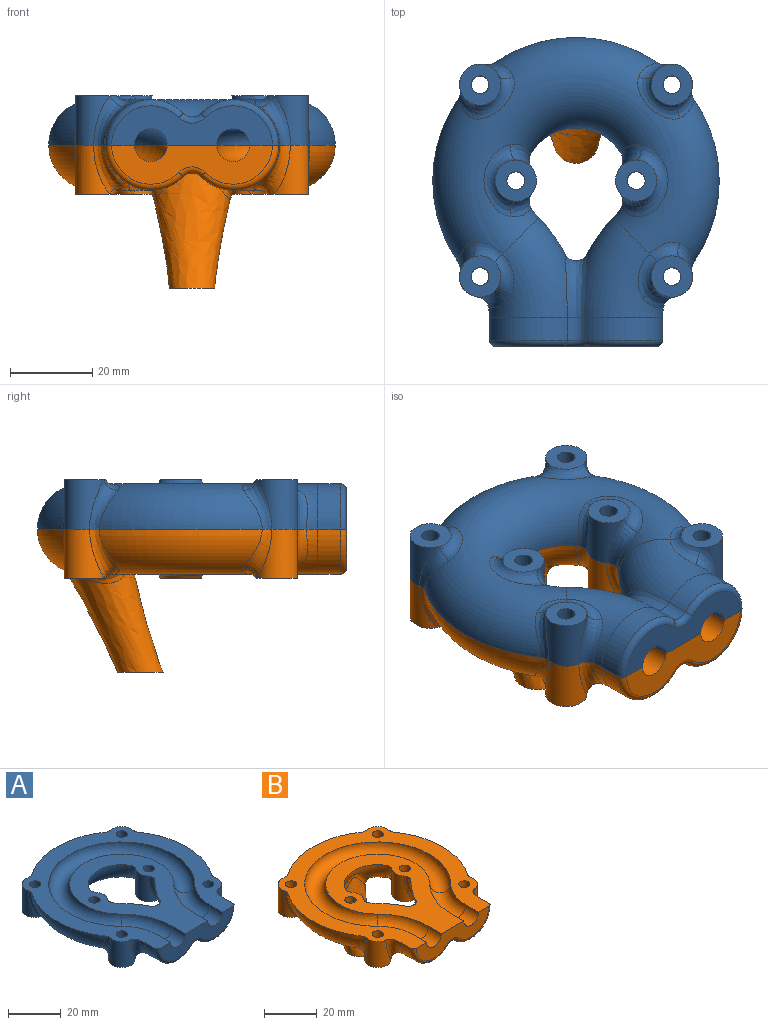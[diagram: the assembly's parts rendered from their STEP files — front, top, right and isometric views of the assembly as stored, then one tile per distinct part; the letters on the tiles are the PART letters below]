
ASSEMBLY  parts=2 mates=1
PART A: 56 faces, bbox 75.6x78.3x20.8 mm
  f0: plane 60.28x39.81mm, normal (0,0,1), area 970.4mm2, adj f2,f3,f4,f6,f7,f8,f9,f10
  f1: plane 75.05x69.58mm, normal (0,0,1), area 1332.3mm2, adj f2,f3,f4,f5,f6,f7,f8,f9
  f2: torus R=23.77mm, axis (0,0,-1), area 2757.4mm2, adj f0,f1,f3,f7,f33,f34,f37,f38
  f3: torus R=23.23mm, axis (0,0,1), area 401.1mm2, adj f0,f1,f2,f11,f35,f36,f40
  f4: plane 39x9.5mm, normal (0,-1,0), area 245.2mm2, adj f0,f1,f6,f12,f53,f54,f55
  f5: cylinder r=11mm len=18.86mm, axis (0,1,0), area 143.2mm2, adj f1,f7,f39,f53
  f6: cylinder r=4mm len=8mm, axis (0,1,0), area 88mm2, adj f0,f1,f4,f8
  f7: torus R=23.23mm, axis (0,0,1), area 401.1mm2, adj f0,f1,f2,f5,f31,f32,f40
  f8: torus R=23.23mm, axis (0,0,1), area 229.3mm2, adj f0,f1,f6,f9
  f9: torus R=23.77mm, axis (0,0,-1), area 1407.4mm2, adj f0,f1,f8,f10
  f10: torus R=23.23mm, axis (0,0,1), area 229.3mm2, adj f0,f1,f9,f12
  f11: cylinder r=11mm len=18.86mm, axis (0,-1,0), area 143.2mm2, adj f1,f3,f39,f55
  f12: cylinder r=4mm len=8mm, axis (0,-1,0), area 88mm2, adj f0,f1,f4,f10
  f13: cylinder r=5mm len=12mm, axis (0,0,1), area 156.2mm2, adj f1,f14,f50,f52
  f14: plane 10.36x10.36mm, normal (0,0,-1), area 64mm2, adj f13,f30,f51
  f15: cylinder r=5mm len=12mm, axis (0,0,1), area 133.3mm2, adj f1,f16,f35,f38
  f16: plane 10.38x10.38mm, normal (0,0,-1), area 64mm2, adj f15,f29,f36,f37
  f17: cylinder r=5mm len=12mm, axis (0,0,1), area 156.2mm2, adj f1,f18,f47,f49
  f18: plane 10.36x10.36mm, normal (0,0,-1), area 64mm2, adj f17,f28,f48
  f19: cylinder r=5mm len=12mm, axis (0,0,1), area 133.3mm2, adj f1,f20,f31,f34
  f20: plane 10.38x10.38mm, normal (0,0,-1), area 64mm2, adj f19,f27,f32,f33
  f21: cylinder r=5mm len=12mm, axis (0,0,1), area 111.7mm2, adj f0,f22,f44,f46
  f22: plane 10.39x10.39mm, normal (0,0,-1), area 64mm2, adj f21,f26,f45
  f23: cylinder r=5mm len=12mm, axis (0,0,1), area 111.7mm2, adj f0,f24,f41,f43
  f24: plane 10.39x10.39mm, normal (0,0,-1), area 64mm2, adj f23,f25,f42
  f25: cylinder r=2.15mm len=12mm, axis (0,0,1), area 162.1mm2, adj f0,f24
  f26: cylinder r=2.15mm len=12mm, axis (0,0,1), area 162.1mm2, adj f0,f22
  f27: cylinder r=2.15mm len=12mm, axis (0,0,1), area 162.1mm2, adj f1,f20
  f28: cylinder r=2.15mm len=12mm, axis (0,0,1), area 162.1mm2, adj f1,f18
  f29: cylinder r=2.15mm len=12mm, axis (0,0,1), area 162.1mm2, adj f1,f16
  f30: cylinder r=2.15mm len=12mm, axis (0,0,1), area 162.1mm2, adj f1,f14
  f31: bspline ~14.01x8.25mm, area 52.2mm2, adj f1,f7,f19,f32
  f32: bspline ~10.86x4.77mm, area 35.4mm2, adj f7,f20,f31,f33
  f33: bspline ~8.15x5.06mm, area 24.6mm2, adj f2,f20,f32,f34
  f34: bspline ~14.58x7.27mm, area 41.1mm2, adj f1,f2,f19,f33
  f35: bspline ~14.01x8.25mm, area 52.2mm2, adj f1,f3,f15,f36
  f36: bspline ~10.86x4.77mm, area 35.4mm2, adj f3,f16,f35,f37
  f37: bspline ~8.15x5.06mm, area 24.6mm2, adj f2,f16,f36,f38
  f38: bspline ~13.38x7.26mm, area 41.1mm2, adj f1,f2,f15,f37
  f39: cylinder r=3mm len=5.5mm, axis (0,1,0), area 26.3mm2, adj f5,f11,f40,f54
  f40: bspline ~17.07x8mm, area 95.7mm2, adj f0,f3,f7,f39
  f41: bspline ~13.11x6.17mm, area 51.8mm2, adj f0,f2,f23,f42
  f42: bspline ~17.49x7.8mm, area 70.2mm2, adj f2,f24,f41,f43
  f43: bspline ~13.83x6.12mm, area 51.8mm2, adj f0,f2,f23,f42
  f44: bspline ~12.91x5.98mm, area 51.8mm2, adj f0,f2,f21,f45
  f45: bspline ~17.49x7.8mm, area 70.2mm2, adj f2,f22,f44,f46
  f46: bspline ~14.07x6.28mm, area 51.8mm2, adj f0,f2,f21,f45
  f47: bspline ~13.12x7.1mm, area 41.1mm2, adj f1,f2,f17,f48
  f48: bspline ~10.75x10.58mm, area 49.3mm2, adj f2,f18,f47,f49
  f49: bspline ~13.53x7.19mm, area 41.1mm2, adj f1,f2,f17,f48
  f50: bspline ~13.12x7.1mm, area 41.1mm2, adj f1,f2,f13,f51
  f51: bspline ~10.75x10.58mm, area 49.3mm2, adj f2,f14,f50,f52
  f52: bspline ~13.53x7.2mm, area 41.1mm2, adj f1,f2,f13,f51
  f53: torus R=9.5mm, axis (0,1,0), area 58.3mm2, adj f1,f4,f5,f54
  f54: torus R=4.5mm, axis (0,1,0), area 13.3mm2, adj f4,f39,f53,f55
  f55: torus R=9.5mm, axis (0,1,0), area 58.3mm2, adj f1,f4,f11,f54
PART B: 59 faces, bbox 75.6x78.3x43 mm
  f0: plane 60.28x39.81mm, normal (0,0,1), area 970.4mm2, adj f2,f3,f4,f6,f7,f8,f9,f10
  f1: plane 75.05x69.58mm, normal (0,0,1), area 1332.3mm2, adj f2,f3,f4,f5,f6,f7,f8,f9
  f2: torus R=23.77mm, axis (0,0,-1), area 2365.6mm2, adj f0,f1,f3,f7,f33,f34,f37,f38
  f3: torus R=23.23mm, axis (0,0,1), area 410.3mm2, adj f0,f1,f2,f11,f35,f36,f40
  f4: plane 39x9.5mm, normal (0,-1,0), area 245.2mm2, adj f0,f1,f6,f12,f56,f57,f58
  f5: cylinder r=11mm len=18.86mm, axis (0,1,0), area 143.2mm2, adj f1,f7,f39,f56
  f6: cylinder r=4mm len=8mm, axis (0,1,0), area 88mm2, adj f0,f1,f4,f8
  f7: torus R=23.23mm, axis (0,0,1), area 410.3mm2, adj f0,f1,f2,f5,f31,f32,f40
  f8: torus R=23.23mm, axis (0,0,1), area 229.3mm2, adj f0,f1,f6,f9
  f9: torus R=23.77mm, axis (0,0,-1), area 1407.4mm2, adj f0,f1,f8,f10
  f10: torus R=23.23mm, axis (0,0,1), area 229.3mm2, adj f0,f1,f9,f12
  f11: cylinder r=11mm len=18.86mm, axis (0,-1,0), area 143.2mm2, adj f1,f3,f39,f58
  f12: cylinder r=4mm len=8mm, axis (0,-1,0), area 88mm2, adj f0,f1,f4,f10
  f13: cylinder r=5mm len=12mm, axis (0,0,1), area 156.2mm2, adj f1,f14,f50,f52
  f14: plane 10.36x10.36mm, normal (0,0,-1), area 64mm2, adj f13,f30,f51
  f15: cylinder r=5mm len=12mm, axis (0,0,1), area 133.3mm2, adj f1,f16,f35,f38
  f16: plane 10.38x10.38mm, normal (0,0,-1), area 64mm2, adj f15,f29,f36,f37
  f17: cylinder r=5mm len=12mm, axis (0,0,1), area 156.2mm2, adj f1,f18,f47,f49
  f18: plane 10.36x10.36mm, normal (0,0,-1), area 64mm2, adj f17,f28,f48
  f19: cylinder r=5mm len=12mm, axis (0,0,1), area 133.3mm2, adj f1,f20,f31,f34
  f20: plane 10.38x10.38mm, normal (0,0,-1), area 64mm2, adj f19,f27,f32,f33
  f21: cylinder r=5mm len=12mm, axis (0,0,1), area 111.7mm2, adj f0,f22,f44,f46
  f22: plane 10.39x10.39mm, normal (0,0,-1), area 64mm2, adj f21,f26,f45
  f23: cylinder r=5mm len=12mm, axis (0,0,1), area 111.7mm2, adj f0,f24,f41,f43
  f24: plane 10.39x10.39mm, normal (0,0,-1), area 64mm2, adj f23,f25,f42
  f25: cylinder r=2.15mm len=12mm, axis (0,0,1), area 162.1mm2, adj f0,f24
  f26: cylinder r=2.15mm len=12mm, axis (0,0,1), area 162.1mm2, adj f0,f22
  f27: cylinder r=2.15mm len=12mm, axis (0,0,1), area 162.1mm2, adj f1,f20
  f28: cylinder r=2.15mm len=12mm, axis (0,0,1), area 162.1mm2, adj f1,f18
  f29: cylinder r=2.15mm len=12mm, axis (0,0,1), area 162.1mm2, adj f1,f16
  f30: cylinder r=2.15mm len=12mm, axis (0,0,1), area 162.1mm2, adj f1,f14
  f31: bspline ~14.01x8.25mm, area 52.2mm2, adj f1,f7,f19,f32
  f32: bspline ~10.86x4.77mm, area 35.4mm2, adj f7,f20,f31,f33
  f33: bspline ~8.15x5.06mm, area 24.6mm2, adj f2,f20,f32,f34
  f34: bspline ~14.58x7.27mm, area 41.1mm2, adj f1,f2,f19,f33
  f35: bspline ~14.01x8.25mm, area 52.2mm2, adj f1,f3,f15,f36
  f36: bspline ~10.86x4.77mm, area 35.4mm2, adj f3,f16,f35,f37
  f37: bspline ~8.15x5.06mm, area 24.6mm2, adj f2,f16,f36,f38
  f38: bspline ~13.38x7.26mm, area 41.1mm2, adj f1,f2,f15,f37
  f39: cylinder r=3mm len=5.5mm, axis (0,1,0), area 26.3mm2, adj f5,f11,f40,f57
  f40: bspline ~17.07x8mm, area 95.7mm2, adj f0,f3,f7,f39
  f41: bspline ~13.11x6.17mm, area 51.8mm2, adj f0,f2,f23,f42
  f42: bspline ~17.49x7.8mm, area 70.2mm2, adj f2,f24,f41,f43
  f43: bspline ~13.83x6.12mm, area 51.8mm2, adj f0,f2,f23,f42
  f44: bspline ~12.91x5.98mm, area 51.8mm2, adj f0,f2,f21,f45
  f45: bspline ~17.49x7.8mm, area 70.2mm2, adj f2,f22,f44,f46
  f46: bspline ~14.07x6.28mm, area 51.8mm2, adj f0,f2,f21,f45
  f47: bspline ~13.12x7.1mm, area 41.1mm2, adj f1,f2,f17,f48
  f48: bspline ~10.75x10.58mm, area 49.3mm2, adj f2,f18,f47,f49
  f49: bspline ~13.53x7.19mm, area 41.1mm2, adj f1,f2,f17,f48
  f50: bspline ~13.12x7.1mm, area 41.1mm2, adj f1,f2,f13,f51
  f51: bspline ~10.75x10.58mm, area 49.3mm2, adj f2,f14,f50,f52
  f52: bspline ~13.53x7.2mm, area 41.1mm2, adj f1,f2,f13,f51
  f53: bspline ~31.3x27.46mm, area 1113.2mm2, adj f54,f55
  f54: plane 11.02x11.02mm, normal (0,0,-1), area 95mm2, adj f53
  f55: bspline ~24.99x16.32mm, area 200.8mm2, adj f2,f53
  f56: torus R=9.5mm, axis (0,1,0), area 58.3mm2, adj f1,f4,f5,f57
  f57: torus R=4.5mm, axis (0,1,0), area 13.3mm2, adj f4,f39,f56,f58
  f58: torus R=9.5mm, axis (0,1,0), area 58.3mm2, adj f1,f4,f11,f57
PLACE A rot(axis=(0,1,0),180deg) t=(20,0,0)mm
PLACE B at identity fixed
MATE fastened B.f21 <-> A.f23  axis (0,0,1) through (-4.62,40.23,0)mm
